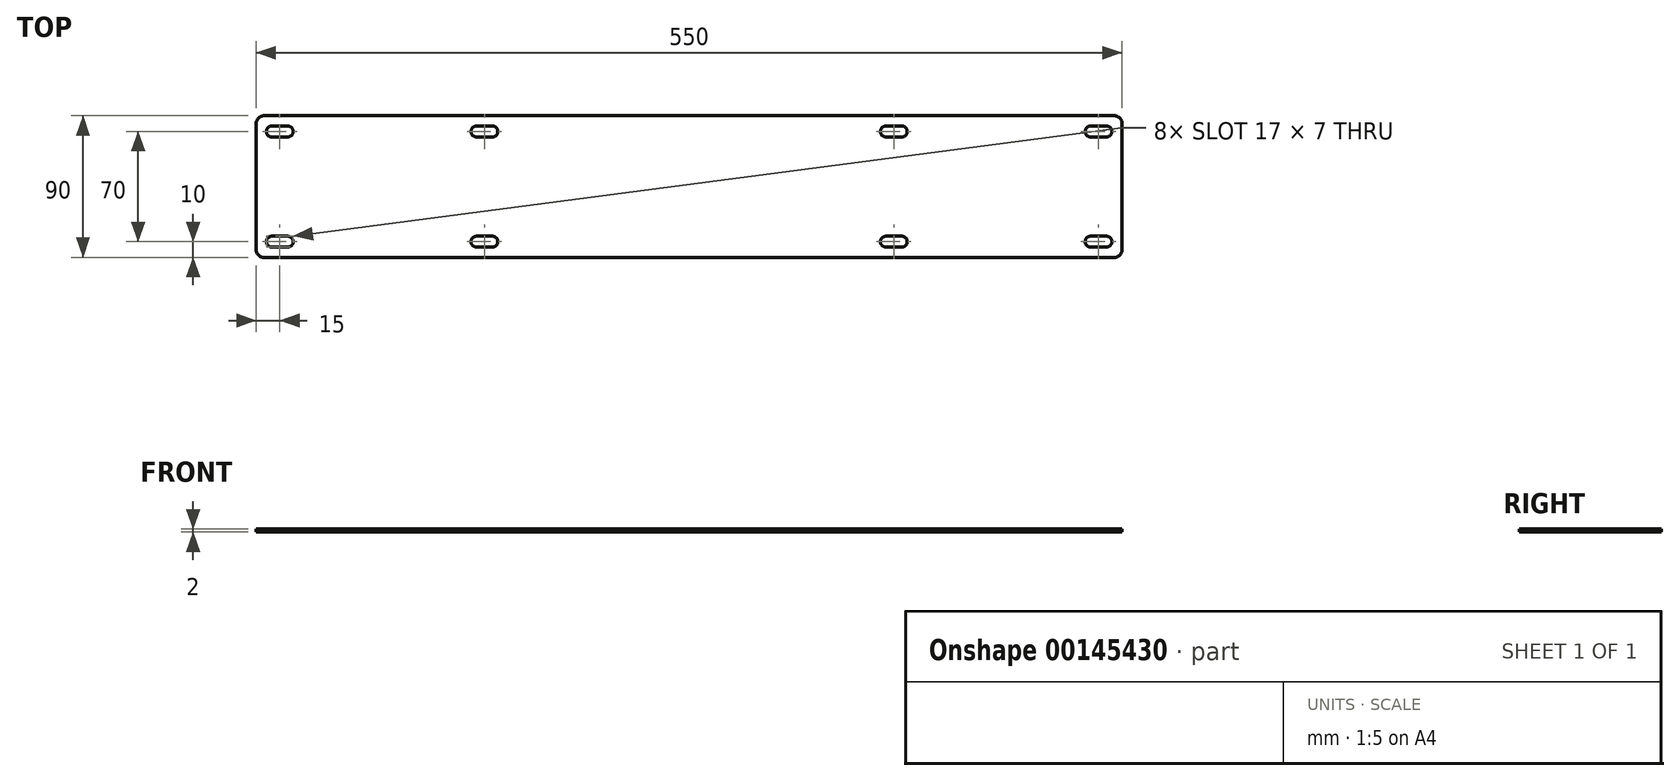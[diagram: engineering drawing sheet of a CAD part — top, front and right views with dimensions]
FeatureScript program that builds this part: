
annotation { "Feature Type Name" : "Feature", "Feature Type Description" : "" }
export const myFeature = defineFeature(function(context is Context, id is Id, definition is map)
    precondition{}
    {
        {
            var Q0;
            Q0=qCreatedBy(makeId("Top.planeOp"),FACE);
            var sketch = newSketch(context, id + "F0", { "sketchPlane" : qUnion([Q0])});
            skLineSegment(sketch, "E0.bottom", {"start": v(270, 45) * mm, "end": v(-270, 45) * mm});
            skLineSegment(sketch, "E0.top", {"start": v(270, -45) * mm, "end": v(-270, -45) * mm});
            skLineSegment(sketch, "E0.left", {"start": v(275, 40) * mm, "end": v(275, -40) * mm});
            skLineSegment(sketch, "E0.right", {"start": v(-275, 40) * mm, "end": v(-275, -40) * mm});
            skPoint(sketch, "E0.middle", {"position": v(0, 0) * mm});
            skCircle(sketch, "E1", {"center": v(-265, 35) * mm, "radius": 3.5 * mm});
            skCircle(sketch, "E2", {"center": v(-255, 35) * mm, "radius": 3.5 * mm});
            skLineSegment(sketch, "E3", {"start": v(-255, 38.5) * mm, "end": v(-265, 38.5) * mm});
            skLineSegment(sketch, "E4", {"start": v(-255, 31.5) * mm, "end": v(-265, 31.5) * mm});
            skLineSegment(sketch, "E5.MirrorCS", {"start": v(-255, -38.5) * mm, "end": v(-265, -38.5) * mm});
            skCircle(sketch, "E6.MirrorC", {"center": v(-255, -35) * mm, "radius": 3.5 * mm});
            skLineSegment(sketch, "E7.MirrorCS", {"start": v(-255, -31.5) * mm, "end": v(-265, -31.5) * mm});
            skCircle(sketch, "E8.MirrorC", {"center": v(-265, -35) * mm, "radius": 3.5 * mm});
            skLineSegment(sketch, "E9.MirrorCS", {"start": v(255, 38.5) * mm, "end": v(265, 38.5) * mm});
            skCircle(sketch, "E10.MirrorC", {"center": v(265, 35) * mm, "radius": 3.5 * mm});
            skLineSegment(sketch, "E11.MirrorCS", {"start": v(255, 31.5) * mm, "end": v(265, 31.5) * mm});
            skCircle(sketch, "E12.MirrorC", {"center": v(255, 35) * mm, "radius": 3.5 * mm});
            skLineSegment(sketch, "E13.MirrorCS", {"start": v(255, -31.5) * mm, "end": v(265, -31.5) * mm});
            skCircle(sketch, "E14.MirrorC", {"center": v(255, -35) * mm, "radius": 3.5 * mm});
            skLineSegment(sketch, "E15.MirrorCS", {"start": v(255, -38.5) * mm, "end": v(265, -38.5) * mm});
            skCircle(sketch, "E16.MirrorC", {"center": v(265, -35) * mm, "radius": 3.5 * mm});
            skPoint(sketch, "E17.visualSharp", {"position": v(-275, 45) * mm});
            skArc(sketch, "E17.filletArc", {"start": v(-270, 45) * mm, "mid": v(-273.54, 43.54) * mm, "end": v(-275, 40) * mm});
            skPoint(sketch, "E18.visualSharp", {"position": v(-275, -45) * mm});
            skArc(sketch, "E18.filletArc", {"start": v(-275, -40) * mm, "mid": v(-273.54, -43.54) * mm, "end": v(-270, -45) * mm});
            skPoint(sketch, "E19.visualSharp", {"position": v(275, 45) * mm});
            skArc(sketch, "E19.filletArc", {"start": v(275, 40) * mm, "mid": v(273.54, 43.54) * mm, "end": v(270, 45) * mm});
            skPoint(sketch, "E20.visualSharp", {"position": v(275, -45) * mm});
            skArc(sketch, "E20.filletArc", {"start": v(270, -45) * mm, "mid": v(273.54, -43.54) * mm, "end": v(275, -40) * mm});
            skCircle(sketch, "E21", {"center": v(-135, 35) * mm, "radius": 3.5 * mm});
            skCircle(sketch, "E22", {"center": v(-125, 35) * mm, "radius": 3.5 * mm});
            skLineSegment(sketch, "E23", {"start": v(-125, 38.5) * mm, "end": v(-135, 38.5) * mm});
            skLineSegment(sketch, "E24", {"start": v(-125, 31.5) * mm, "end": v(-135, 31.5) * mm});
            skLineSegment(sketch, "E25.MirrorCS", {"start": v(-125, -38.5) * mm, "end": v(-135, -38.5) * mm});
            skCircle(sketch, "E26.MirrorC", {"center": v(-125, -35) * mm, "radius": 3.5 * mm});
            skLineSegment(sketch, "E27.MirrorCS", {"start": v(-125, -31.5) * mm, "end": v(-135, -31.5) * mm});
            skCircle(sketch, "E28.MirrorC", {"center": v(-135, -35) * mm, "radius": 3.5 * mm});
            skCircle(sketch, "E29.MirrorC", {"center": v(125, 35) * mm, "radius": 3.5 * mm});
            skLineSegment(sketch, "E30.MirrorCS", {"start": v(125, 38.5) * mm, "end": v(135, 38.5) * mm});
            skLineSegment(sketch, "E31.MirrorCS", {"start": v(125, 31.5) * mm, "end": v(135, 31.5) * mm});
            skCircle(sketch, "E32.MirrorC", {"center": v(135, 35) * mm, "radius": 3.5 * mm});
            skLineSegment(sketch, "E33.MirrorCS", {"start": v(125, -31.5) * mm, "end": v(135, -31.5) * mm});
            skCircle(sketch, "E34.MirrorC", {"center": v(125, -35) * mm, "radius": 3.5 * mm});
            skLineSegment(sketch, "E35.MirrorCS", {"start": v(125, -38.5) * mm, "end": v(135, -38.5) * mm});
            skCircle(sketch, "E36.MirrorC", {"center": v(135, -35) * mm, "radius": 3.5 * mm});
            skSolve(sketch);
        }
        {
            var Q0;
            Q0 = qSketchRegion(id + "F0", true);
            extrude(context, id + "F1", {"entities" : qUnion([Q0]), "depth" : 2 * mm});
        }
    });
